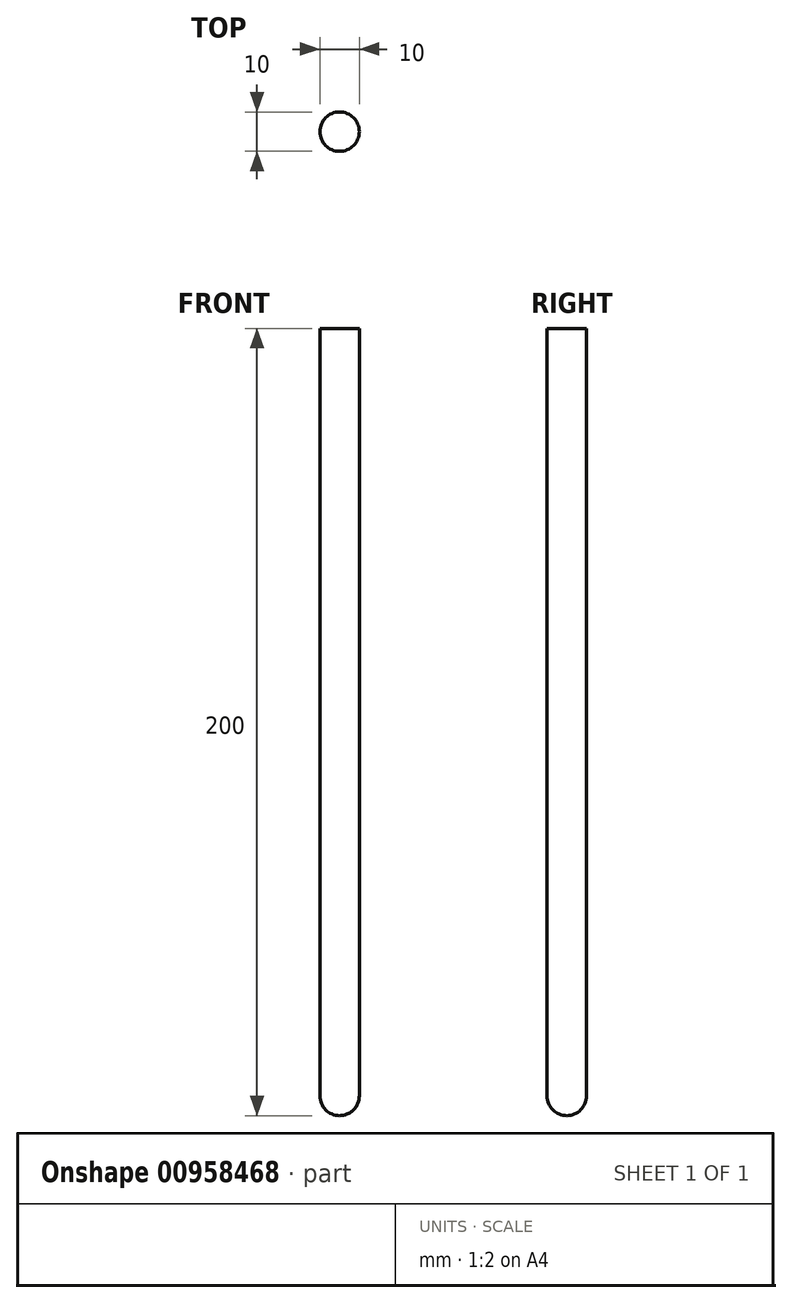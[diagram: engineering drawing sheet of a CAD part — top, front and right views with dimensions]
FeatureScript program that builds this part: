
annotation { "Feature Type Name" : "Feature", "Feature Type Description" : "" }
export const myFeature = defineFeature(function(context is Context, id is Id, definition is map)
    precondition{}
    {
        {
            var Q0;
            Q0=qCreatedBy(makeId("Top.planeOp"),FACE);
            var sketch = newSketch(context, id + "F0", { "sketchPlane" : qUnion([Q0])});
            skCircle(sketch, "E0", {"center": v(0, 0) * mm, "radius": 5 * mm});
            skSolve(sketch);
        }
        {
            var Q0;
            Q0=makeQuery(id+"F0.imprint","IMPRINT",FACE,{"disambiguationData":[TD([[makeQuery(id+"F0.imprint","IMPRINT",EDGE,{"derivedFrom":sQuery(id+"F0.wireOp",EDGE,"E0")}),1.0]])]});
            extrude(context, id + "F1", {"entities" : qUnion([Q0]), "oppositeDirection" : true, "depth" : 200 * mm, "offsetDistance" : 25 * mm});
        }
        {
            var Q0;
            Q0=makeQuery(id+"F1.opExtrude","CAP_FACE",FACE,{"disambiguationData":[OSD([sQuery(id+"F0.wireOp",EDGE,"E0")])],"isStart":false});
            fillet(context, id + "F2", {"entities" : qUnion([Q0]), "radius" : 5 * mm, "allowEdgeOverflow" : false});
        }
    });
